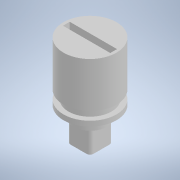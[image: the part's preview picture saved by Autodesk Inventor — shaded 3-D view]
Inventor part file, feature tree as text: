
AUTODESK INVENTOR PART (.ipt)
format: ipt  version: 2021 (Build 250183000, 183)  size: 152,064 bytes
history: native  units: mm
features: other x7, sketch x3, extrude x2, revolve x1
ambient origin geometry x8: Origin, YZ Plane, XZ Plane, XY Plane, X Axis, Y Axis, Z Axis, Center Point
bodies: Solid1 (feature_tree)
feature tree (13):
  revolve  "Revolution1"  [1 undecoded]
  extrude  "Extrusion1"  TaperAngle=0.0deg  [1 undecoded]
  extrude  "Extrusion2"  [1 undecoded]
  other  "insert_to_lock_XY"
  other  "insert_to_lock_YZ"
  other  "insert_to_lock_ZX"
  other  "insert_to_lock_X"
  other  "insert_to_lock_Y"
  other  "insert_to_lock_Z"
  other  "insert_to_lock_Center"
  sketch  "Sketch_1"  dims[d0=360.0deg d1=6.5mm d2=0.0mm]
  sketch  "Sketch_2"  dims[d3=2.71mm d4=0.0mm d5=0.0mm]
  sketch  "Sketch_3"
note: 3 required parameter values undecoded (feature->parameter linkage not recoverable at this tier; creation-order binding heuristic only, values carry confidence <= 0.55)